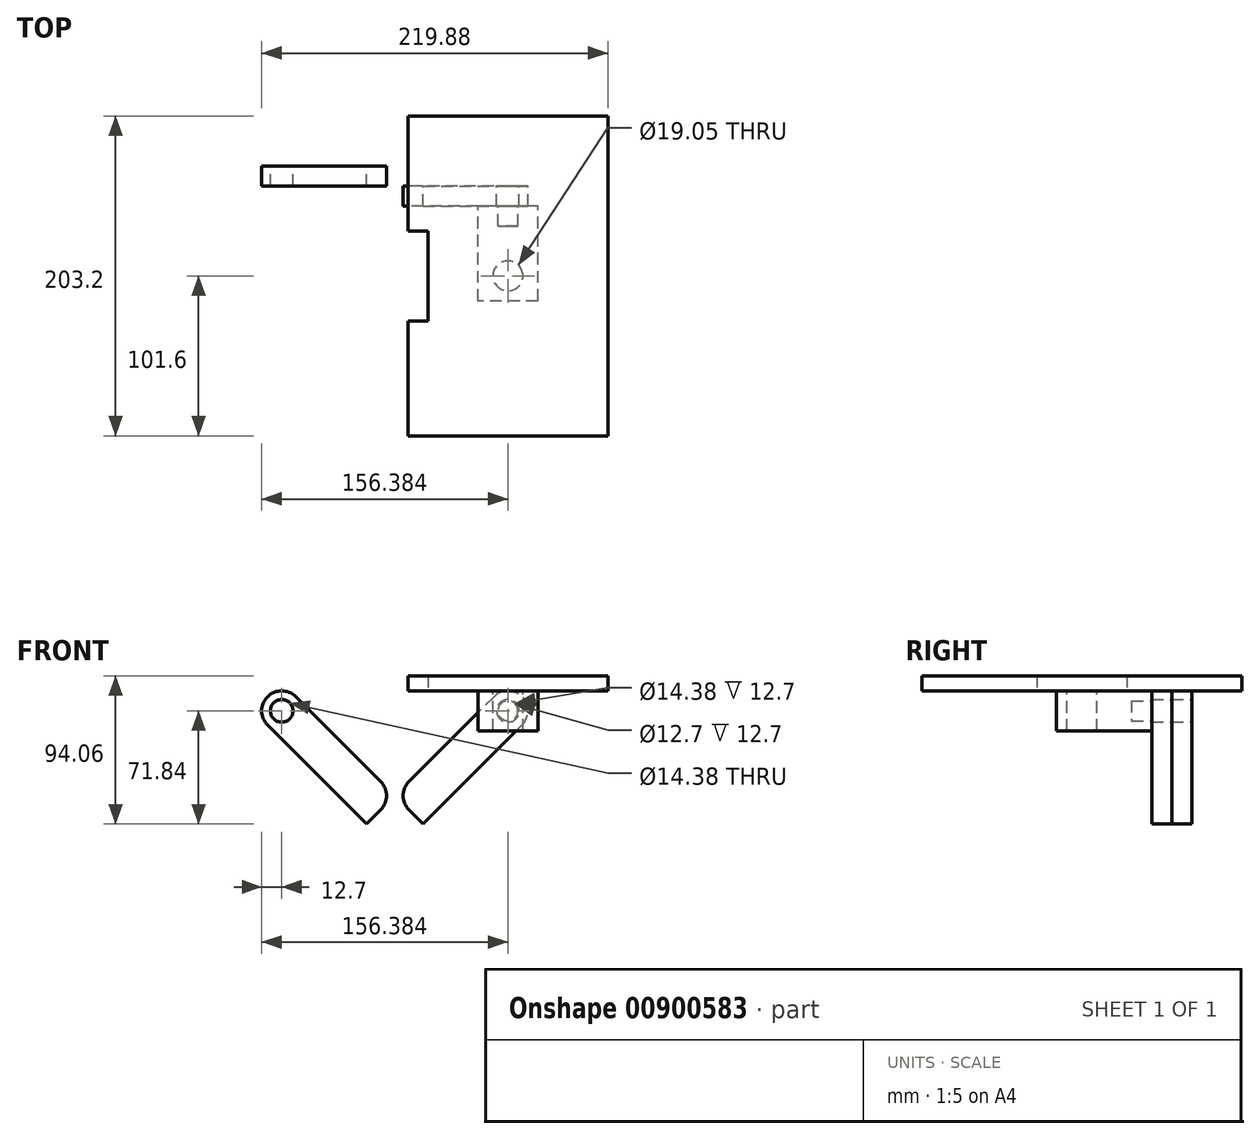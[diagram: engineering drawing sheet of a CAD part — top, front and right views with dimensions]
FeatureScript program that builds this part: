
annotation { "Feature Type Name" : "Feature", "Feature Type Description" : "" }
export const myFeature = defineFeature(function(context is Context, id is Id, definition is map)
    precondition{}
    {
        {
            var Q0;
            Q0=qCreatedBy(makeId("Front.planeOp"),FACE);
            var sketch = newSketch(context, id + "F0", { "sketchPlane" : qUnion([Q0])});
            skLineSegment(sketch, "E0", {"start": v(0, 0) * mm, "end": v(-17.96, -17.96) * mm});
            skLineSegment(sketch, "E1", {"start": v(-17.96, -17.96) * mm, "end": v(71.84, -107.76) * mm});
            skLineSegment(sketch, "E2", {"start": v(71.84, -107.76) * mm, "end": v(89.8, -89.8) * mm});
            skLineSegment(sketch, "E3", {"start": v(89.8, -89.8) * mm, "end": v(0, 0) * mm});
            skCircle(sketch, "E4", {"center": v(71.84, -89.8) * mm, "radius": 7.19 * mm});
            skLineSegment(sketch, "E5", {"start": v(53.88, -89.8) * mm, "end": v(71.84, -107.76) * mm});
            skLineSegment(sketch, "E6", {"start": v(71.84, -107.76) * mm, "end": v(161.64, -17.96) * mm});
            skLineSegment(sketch, "E7", {"start": v(161.64, -17.96) * mm, "end": v(143.68, 0) * mm});
            skLineSegment(sketch, "E8", {"start": v(143.68, 0) * mm, "end": v(53.88, -89.8) * mm});
            skCircle(sketch, "E9", {"center": v(0, -17.96) * mm, "radius": 7.19 * mm});
            skCircle(sketch, "E10", {"center": v(143.68, -17.96) * mm, "radius": 7.19 * mm});
            skSolve(sketch);
        }
        {
            var Q0;
            {var subQ4=sQuery(id+"F0.wireOp",EDGE,"E0");Q0=makeQuery(id+"F0.imprint","IMPRINT",FACE,{"disambiguationData":[TD([[makeQuery(id+"F0.imprint","IMPRINT",EDGE,{"derivedFrom":subQ4}),1.0]])]});}
            var Q1;
            {var subQ3=sQuery(id+"F0.wireOp",EDGE,"E5");Q1=makeQuery(id+"F0.imprint","IMPRINT",FACE,{"disambiguationData":[TD([[makeQuery(id+"F0.imprint","IMPRINT",EDGE,{"derivedFrom":subQ3}),1.0]])]});}
            extrude(context, id + "F1", {"entities" : qUnion([Q0, Q1]), "depth" : 12.7 * mm, "offsetDistance" : 25.4 * mm});
        }
        {
            var Q0;
            {var subQ1=sQuery(id+"F0.wireOp",EDGE,"E7");Q0=makeQuery(id+"F0.imprint","IMPRINT",FACE,{"disambiguationData":[TD([[makeQuery(id+"F0.imprint","IMPRINT",EDGE,{"derivedFrom":subQ1}),1.0]])]});}
            var Q1;
            {var subQ3=sQuery(id+"F0.wireOp",EDGE,"E5");Q1=makeQuery(id+"F0.imprint","IMPRINT",FACE,{"disambiguationData":[TD([[makeQuery(id+"F0.imprint","IMPRINT",EDGE,{"derivedFrom":subQ3}),1.0]])]});}
            extrude(context, id + "F2", {"entities" : qUnion([Q0, Q1]), "depth" : 25.4 * mm, "offsetDistance" : 25.4 * mm, "hasSecondDirection" : true, "secondDirectionOppositeDirection" : false, "secondDirectionDepth" : 12.7 * mm});
        }
        {
            var Q0;
            Q0=makeQuery(id+"F2.opExtrude","SWEPT_EDGE",EDGE,{"disambiguationData":[OSD([sQuery(id+"F0.wireOp",EDGE,"E7"),sQuery(id+"F0.wireOp",EDGE,"E8")])]});
            var Q1;
            Q1=makeQuery(id+"F2.opExtrude","SWEPT_EDGE",EDGE,{"disambiguationData":[OSD([sQuery(id+"F0.wireOp",EDGE,"E6"),sQuery(id+"F0.wireOp",EDGE,"E7")])]});
            var Q2;
            Q2=makeQuery(id+"F1.opExtrude","SWEPT_EDGE",EDGE,{"disambiguationData":[OSD([sQuery(id+"F0.wireOp",EDGE,"E3"),sQuery(id+"F0.wireOp",EDGE,"E6")])]});
            var Q3;
            Q3=makeQuery(id+"F1.opExtrude","SWEPT_EDGE",EDGE,{"disambiguationData":[OSD([sQuery(id+"F0.wireOp",EDGE,"E5"),sQuery(id+"F0.wireOp",EDGE,"E6")])]});
            var Q4;
            Q4=makeQuery(id+"F2.opExtrude","SWEPT_EDGE",EDGE,{"disambiguationData":[OSD([sQuery(id+"F0.wireOp",EDGE,"E1"),sQuery(id+"F0.wireOp",EDGE,"E5"),sQuery(id+"F0.wireOp",EDGE,"E8")])]});
            var Q5;
            Q5=makeQuery(id+"F2.opExtrude","SWEPT_EDGE",EDGE,{"disambiguationData":[OSD([sQuery(id+"F0.wireOp",EDGE,"E5"),sQuery(id+"F0.wireOp",EDGE,"E6")])]});
            var Q6;
            Q6=makeQuery(id+"F1.opExtrude","SWEPT_EDGE",EDGE,{"disambiguationData":[OSD([sQuery(id+"F0.wireOp",EDGE,"E0"),sQuery(id+"F0.wireOp",EDGE,"E3")])]});
            var Q7;
            Q7=makeQuery(id+"F1.opExtrude","SWEPT_EDGE",EDGE,{"disambiguationData":[OSD([sQuery(id+"F0.wireOp",EDGE,"E0"),sQuery(id+"F0.wireOp",EDGE,"E1")])]});
            fillet(context, id + "F3", {"entities" : qUnion([Q0, Q1, Q2, Q3, Q4, Q5, Q6, Q7]), "radius" : 12.7 * mm, "tangentPropagation" : true, "allowEdgeOverflow" : false});
        }
        {
            var Q0;
            {var subQ1=sQuery(id+"F0.wireOp",EDGE,"E7");Q0=makeQuery(id+"F0.imprint","IMPRINT",FACE,{"disambiguationData":[TD([[makeQuery(id+"F0.imprint","IMPRINT",EDGE,{"derivedFrom":subQ1}),1.0]])]});}
            var sketch = newSketch(context, id + "F4", { "sketchPlane" : qUnion([Q0])});
            skLineSegment(sketch, "E11.bottom", {"start": v(162.73, -5.26) * mm, "end": v(124.63, -5.26) * mm});
            skLineSegment(sketch, "E11.top", {"start": v(162.73, -30.66) * mm, "end": v(124.63, -30.66) * mm});
            skLineSegment(sketch, "E11.left", {"start": v(162.73, -5.26) * mm, "end": v(162.73, -30.66) * mm});
            skLineSegment(sketch, "E11.right", {"start": v(124.63, -5.26) * mm, "end": v(124.63, -30.66) * mm});
            skSolve(sketch);
        }
        {
            var Q0;
            Q0 = qSketchRegion(id + "F4", true);
            extrude(context, id + "F5", {"entities" : qUnion([Q0]), "operationType" : NewBodyOperationType.ADD, "depth" : 85.72 * mm, "offsetDistance" : 25.4 * mm, "hasSecondDirection" : true, "secondDirectionOppositeDirection" : false, "secondDirectionDepth" : 25.4 * mm});
        }
        {
            var Q0;
            Q0=makeQuery(id+"F0.imprint","IMPRINT",FACE,{"disambiguationData":[TD([[makeQuery(id+"F0.imprint","IMPRINT",EDGE,{"derivedFrom":sQuery(id+"F0.wireOp",EDGE,"E10")}),1.0]])]});
            extrude(context, id + "F6", {"entities" : qUnion([Q0]), "operationType" : NewBodyOperationType.REMOVE, "oppositeDirection" : true, "depth" : 19.05 * mm, "offsetDistance" : 25.4 * mm});
        }
        {
            var Q0;
            Q0=makeQuery(id+"F5.opExtrude","SWEPT_FACE",FACE,{"disambiguationData":[OSD([sQuery(id+"F4.wireOp",EDGE,"E11.bottom")])]});
            var sketch = newSketch(context, id + "F7", { "sketchPlane" : qUnion([Q0])});
            skCircle(sketch, "E12", {"center": v(143.68, -69.85) * mm, "radius": 9.53 * mm});
            skSolve(sketch);
        }
        {
            var Q0;
            Q0 = qSketchRegion(id + "F7", true);
            extrude(context, id + "F8", {"entities" : qUnion([Q0]), "operationType" : NewBodyOperationType.REMOVE, "oppositeDirection" : true, "depth" : 25.4 * mm, "offsetDistance" : 25.4 * mm});
        }
        {
            var Q0;
            {var subQ0=sQuery(id+"F4.wireOp",EDGE,"E11.bottom");var subQ2=sQuery(id+"F0.wireOp",EDGE,"E6");var subQ3=sQuery(id+"F4.wireOp",EDGE,"E11.left");var subQ4=sQuery(id+"F4.wireOp",EDGE,"E11.top");var subQ5=makeQuery(id+"F5.opExtrude","CAP_FACE",FACE,{"disambiguationData":[OSD([subQ0,subQ4,subQ3,sQuery(id+"F4.wireOp",EDGE,"E11.right")])],"isStart":true});Q0=makeQuery(id+"F5.boolean.opBoolean","SPLIT",FACE,{"disambiguationData":[TD([makeQuery(id+"F2.opExtrude","SWEPT_FACE",FACE,{"disambiguationData":[OSD([subQ2])]})])],"derivedFrom":subQ5});}
            var sketch = newSketch(context, id + "F9", { "sketchPlane" : qUnion([Q0])});
            skCircle(sketch, "E13", {"center": v(-143.68, -17.96) * mm, "radius": 6.35 * mm});
            skSolve(sketch);
        }
        {
            var Q0;
            Q0 = qSketchRegion(id + "F9", true);
            extrude(context, id + "F10", {"entities" : qUnion([Q0]), "operationType" : NewBodyOperationType.REMOVE, "oppositeDirection" : true, "depth" : 12.7 * mm, "offsetDistance" : 25.4 * mm});
        }
        {
            var Q0;
            Q0=makeQuery(id+"F5.opExtrude","SWEPT_FACE",FACE,{"disambiguationData":[OSD([sQuery(id+"F4.wireOp",EDGE,"E11.bottom")])]});
            var sketch = newSketch(context, id + "F11", { "sketchPlane" : qUnion([Q0])});
            skLineSegment(sketch, "E14.bottom", {"start": v(80.18, -171.45) * mm, "end": v(207.18, -171.45) * mm});
            skLineSegment(sketch, "E14.right", {"start": v(207.18, 31.75) * mm, "end": v(207.18, -171.45) * mm});
            skLineSegment(sketch, "E15", {"start": v(80.18, -41.28) * mm, "end": v(92.88, -41.28) * mm});
            skLineSegment(sketch, "E16", {"start": v(92.88, -41.28) * mm, "end": v(92.88, -98.43) * mm});
            skLineSegment(sketch, "E17", {"start": v(92.88, -98.43) * mm, "end": v(80.18, -98.43) * mm});
            skLineSegment(sketch, "E18", {"start": v(80.18, -171.45) * mm, "end": v(80.18, -98.43) * mm});
            skLineSegment(sketch, "E19.bottom", {"start": v(-184.15, -44.45) * mm, "end": v(120.65, -44.45) * mm, "construction": true});
            skLineSegment(sketch, "E19.top", {"start": v(-184.15, -95.25) * mm, "end": v(120.65, -95.25) * mm, "construction": true});
            skLineSegment(sketch, "E19.left", {"start": v(-184.15, -44.45) * mm, "end": v(-184.15, -95.25) * mm, "construction": true});
            skLineSegment(sketch, "E19.right", {"start": v(120.65, -44.45) * mm, "end": v(120.65, -95.25) * mm, "construction": true});
            skLineSegment(sketch, "E20.bottom", {"start": v(-88.9, 120.65) * mm, "end": v(25.4, 120.65) * mm, "construction": true});
            skLineSegment(sketch, "E20.top", {"start": v(-88.9, -31.75) * mm, "end": v(25.4, -31.75) * mm, "construction": true});
            skLineSegment(sketch, "E20.left", {"start": v(-88.9, 120.65) * mm, "end": v(-88.9, -31.75) * mm, "construction": true});
            skLineSegment(sketch, "E20.right", {"start": v(25.4, 120.65) * mm, "end": v(25.4, -31.75) * mm, "construction": true});
            skLineSegment(sketch, "E21.bottom", {"start": v(25.4, -31.75) * mm, "end": v(-25.4, -31.75) * mm, "construction": true});
            skLineSegment(sketch, "E21.top", {"start": v(25.4, -12.7) * mm, "end": v(-25.4, -12.7) * mm, "construction": true});
            skLineSegment(sketch, "E21.left", {"start": v(25.4, -31.75) * mm, "end": v(25.4, -12.7) * mm, "construction": true});
            skLineSegment(sketch, "E21.right", {"start": v(-25.4, -31.75) * mm, "end": v(-25.4, -12.7) * mm, "construction": true});
            skLineSegment(sketch, "E22", {"start": v(0, 0) * mm, "end": v(0, -12.7) * mm, "construction": true});
            skLineSegment(sketch, "E23", {"start": v(-31.75, -31.75) * mm, "end": v(-31.75, -44.45) * mm, "construction": true});
            skPoint(sketch, "E23.endSnap0", {"position": v(-31.75, -44.45) * mm});
            skPoint(sketch, "E24", {"position": v(0, -12.7) * mm});
            skLineSegment(sketch, "E25", {"start": v(-31.75, -44.45) * mm, "end": v(-31.75, -95.25) * mm, "construction": true});
            skLineSegment(sketch, "E26", {"start": v(-184.15, -69.85) * mm, "end": v(120.65, -69.85) * mm, "construction": true});
            skPoint(sketch, "E27", {"position": v(92.88, -69.85) * mm});
            skLineSegment(sketch, "E28", {"start": v(80.18, -41.28) * mm, "end": v(80.18, 31.75) * mm});
            skLineSegment(sketch, "E29", {"start": v(80.18, 31.75) * mm, "end": v(207.18, 31.75) * mm});
            skLineSegment(sketch, "E30", {"start": v(92.88, -41.28) * mm, "end": v(92.88, 31.75) * mm, "construction": true});
            skLineSegment(sketch, "E31", {"start": v(92.88, -98.43) * mm, "end": v(92.88, -171.45) * mm, "construction": true});
            skSolve(sketch);
        }
        {
            var Q0;
            Q0 = qSketchRegion(id + "F11", true);
            extrude(context, id + "F12", {"entities" : qUnion([Q0]), "depth" : 9.52 * mm, "offsetDistance" : 25.4 * mm});
        }
        {
            var Q0;
            Q0=makeQuery(id+"F7.imprint","IMPRINT",FACE,{"disambiguationData":[TD([[makeQuery(id+"F7.imprint","IMPRINT",EDGE,{"derivedFrom":sQuery(id+"F7.wireOp",EDGE,"E12")}),1.0]])]});
            extrude(context, id + "F13", {"entities" : qUnion([Q0]), "oppositeDirection" : true, "depth" : 25.4 * mm, "offsetDistance" : 25.4 * mm});
        }
    });
